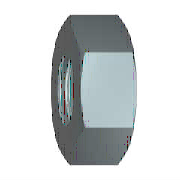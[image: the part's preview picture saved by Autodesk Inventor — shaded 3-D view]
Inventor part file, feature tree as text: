
AUTODESK INVENTOR PART (.ipt)
format: ipt  version: 2025 (Build 290162010, 162A)  size: 164,864 bytes
history: native  units: mm (DEFAULTED — no unit token found)
features: chamfer x1, hole x1, other x1, plane x1
ambient origin geometry x7: Origin, YZ Plane, XZ Plane, X Axis, Y Axis, Z Axis, Center Point
bodies: Solid1 (feature_tree), Body (feature_tree)
feature tree (4):
  chamfer  "Chamfer1"  Distance=6.350853mm
  hole  "Thread"  [1 undecoded]
  other  "Work Axis1"
  plane  "Work Plane1"
note: 1 required parameter value undecoded (feature->parameter linkage not recoverable at this tier; creation-order binding heuristic only, values carry confidence <= 0.55)
